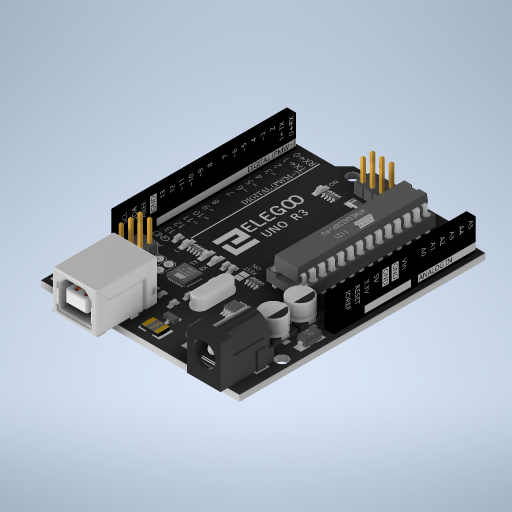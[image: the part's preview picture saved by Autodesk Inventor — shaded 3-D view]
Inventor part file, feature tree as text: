
AUTODESK INVENTOR PART (.ipt)
format: ipt  version: 2024 (Build 280153000, 153)  size: 18,753,536 bytes
history: native  units: in
note: dims shown in document units (in); Inventor stores cm internally (conversion verified against a paired STEP export)
features: other x713, projected_geometry x17, sketch x1
ambient origin geometry x8: Origin, YZ Plane, XZ Plane, XY Plane, X Axis, Y Axis, Z Axis, Center Point
bodies: Solid1 (feature_tree), Solid2 (feature_tree), Solid3 (feature_tree), Solid4 (feature_tree), Solid5 (feature_tree), Solid6 (feature_tree), Solid7 (feature_tree), Solid8 (feature_tree), Solid9 (feature_tree), Solid10 (feature_tree), Solid11 (feature_tree), Solid12 (feature_tree), Solid13 (feature_tree), Solid14 (feature_tree), Solid15 (feature_tree), Solid16 (feature_tree), Solid17 (feature_tree), Solid18 (feature_tree), Solid19 (feature_tree), Solid20 (feature_tree), Solid21 (feature_tree), Solid22 (feature_tree), Solid23 (feature_tree), Solid24 (feature_tree), Solid25 (feature_tree), Solid26 (feature_tree), Solid27 (feature_tree), Solid28 (feature_tree), Solid29 (feature_tree), Solid30 (feature_tree), Solid31 (feature_tree), Solid32 (feature_tree), Solid33 (feature_tree), Solid34 (feature_tree), Solid35 (feature_tree), Solid36 (feature_tree), Solid37 (feature_tree), Solid38 (feature_tree), Solid39 (feature_tree), Solid40 (feature_tree), Solid41 (feature_tree), Solid42 (feature_tree), Solid43 (feature_tree), Solid44 (feature_tree), Solid45 (feature_tree), Solid46 (feature_tree), Solid47 (feature_tree), Solid48 (feature_tree), Solid49 (feature_tree), Solid50 (feature_tree), Solid51 (feature_tree), Solid52 (feature_tree), Solid53 (feature_tree), Solid54 (feature_tree), Solid55 (feature_tree), Solid56 (feature_tree), Solid57 (feature_tree), Solid58 (feature_tree), Solid59 (feature_tree), Solid60 (feature_tree), Solid61 (feature_tree), Solid62 (feature_tree), Solid63 (feature_tree), Solid64 (feature_tree), Solid65 (feature_tree), Solid66 (feature_tree), Solid67 (feature_tree), Solid68 (feature_tree), Solid69 (feature_tree), Solid70 (feature_tree), Solid71 (feature_tree), Solid72 (feature_tree), Solid73 (feature_tree), Solid74 (feature_tree), Solid75 (feature_tree), Solid76 (feature_tree), Solid77 (feature_tree), Solid78 (feature_tree), Solid79 (feature_tree), Solid80 (feature_tree), Solid81 (feature_tree), Solid82 (feature_tree), Solid83 (feature_tree), Solid84 (feature_tree), Solid85 (feature_tree), Solid86 (feature_tree), Solid87 (feature_tree), Solid88 (feature_tree), Solid89 (feature_tree), Solid90 (feature_tree), Solid91 (feature_tree), Solid92 (feature_tree), Solid93 (feature_tree), Solid94 (feature_tree), Solid95 (feature_tree), Solid96 (feature_tree), Solid97 (feature_tree), Solid98 (feature_tree), Solid99 (feature_tree), Solid100 (feature_tree), Solid101 (feature_tree), Solid102 (feature_tree), Solid103 (feature_tree), Solid104 (feature_tree), Solid105 (feature_tree), Solid106 (feature_tree), Solid107 (feature_tree), Solid108 (feature_tree), Solid109 (feature_tree), Solid110 (feature_tree), Solid111 (feature_tree), Solid112 (feature_tree), Solid113 (feature_tree), Solid114 (feature_tree), Solid115 (feature_tree), Solid116 (feature_tree), Solid117 (feature_tree), Solid118 (feature_tree), Solid119 (feature_tree), Solid120 (feature_tree), Solid121 (feature_tree), Solid122 (feature_tree), Solid123 (feature_tree), Solid124 (feature_tree), Solid125 (feature_tree), Solid126 (feature_tree), Solid127 (feature_tree), Solid128 (feature_tree), Solid129 (feature_tree), Solid130 (feature_tree), Solid131 (feature_tree), Solid132 (feature_tree), Solid133 (feature_tree), Solid134 (feature_tree), Solid135 (feature_tree), Solid136 (feature_tree), Solid137 (feature_tree), Solid138 (feature_tree), Solid139 (feature_tree), Solid140 (feature_tree), Solid141 (feature_tree), Solid142 (feature_tree), Solid143 (feature_tree), Solid144 (feature_tree), Solid145 (feature_tree), Solid146 (feature_tree), Solid147 (feature_tree), Solid148 (feature_tree), Solid149 (feature_tree), Solid150 (feature_tree), Solid151 (feature_tree), Solid152 (feature_tree), Solid153 (feature_tree), Solid154 (feature_tree), Solid155 (feature_tree), Solid156 (feature_tree), Solid157 (feature_tree), Solid158 (feature_tree), Solid159 (feature_tree), Solid160 (feature_tree), Solid161 (feature_tree), Solid162 (feature_tree), Solid163 (feature_tree), Solid164 (feature_tree), Solid165 (feature_tree), Solid166 (feature_tree), Solid167 (feature_tree), Solid168 (feature_tree), Solid169 (feature_tree), Solid170 (feature_tree), Solid171 (feature_tree), Solid172 (feature_tree), Solid173 (feature_tree), Solid174 (feature_tree), Solid175 (feature_tree), Solid176 (feature_tree), Solid177 (feature_tree), Solid178 (feature_tree), Solid179 (feature_tree), Solid180 (feature_tree), Solid181 (feature_tree), Solid182 (feature_tree), Solid183 (feature_tree), Solid184 (feature_tree), Solid185 (feature_tree), Solid186 (feature_tree), Solid187 (feature_tree), Solid188 (feature_tree), Solid189 (feature_tree), Solid190 (feature_tree), Solid191 (feature_tree), Solid192 (feature_tree), Solid193 (feature_tree), Solid194 (feature_tree), Solid195 (feature_tree), Solid196 (feature_tree), Solid197 (feature_tree), Solid198 (feature_tree), Solid199 (feature_tree), Solid200 (feature_tree), Solid201 (feature_tree), Solid202 (feature_tree), Solid203 (feature_tree), Solid204 (feature_tree), Solid205 (feature_tree), Solid206 (feature_tree), Solid207 (feature_tree), Solid208 (feature_tree), Solid209 (feature_tree), Solid210 (feature_tree), Solid211 (feature_tree), Solid212 (feature_tree), Solid213 (feature_tree), Solid214 (feature_tree), Solid215 (feature_tree), Solid216 (feature_tree), Solid217 (feature_tree), Solid218 (feature_tree), Solid219 (feature_tree), Solid220 (feature_tree), Solid221 (feature_tree), Solid222 (feature_tree), Solid223 (feature_tree), Solid224 (feature_tree), Solid225 (feature_tree), Solid226 (feature_tree), Solid227 (feature_tree), Solid228 (feature_tree), Solid229 (feature_tree), Solid230 (feature_tree), Solid231 (feature_tree), Solid232 (feature_tree), Solid233 (feature_tree), Solid234 (feature_tree), Solid235 (feature_tree), Solid236 (feature_tree), Solid237 (feature_tree), Solid238 (feature_tree), Solid239 (feature_tree), Solid240 (feature_tree), Solid241 (feature_tree), Solid242 (feature_tree), Solid243 (feature_tree), Solid244 (feature_tree), Solid245 (feature_tree), Solid246 (feature_tree), Solid247 (feature_tree), Solid248 (feature_tree), Solid249 (feature_tree), Solid250 (feature_tree), Solid251 (feature_tree), Solid252 (feature_tree), Solid253 (feature_tree), Solid254 (feature_tree), Solid255 (feature_tree), Solid256 (feature_tree), Solid257 (feature_tree), Solid258 (feature_tree), Solid259 (feature_tree), Solid260 (feature_tree), Solid261 (feature_tree), Solid262 (feature_tree), Solid263 (feature_tree), Solid264 (feature_tree), Solid265 (feature_tree), Solid266 (feature_tree), Solid267 (feature_tree), Solid268 (feature_tree), Solid269 (feature_tree), Solid270 (feature_tree), Solid271 (feature_tree), Solid272 (feature_tree), Solid273 (feature_tree), Solid274 (feature_tree), Solid275 (feature_tree), Solid276 (feature_tree), Solid277 (feature_tree), Solid278 (feature_tree), Solid279 (feature_tree), Solid280 (feature_tree), Solid281 (feature_tree), Solid282 (feature_tree), Solid283 (feature_tree), Solid284 (feature_tree), Solid285 (feature_tree), Solid286 (feature_tree), Solid287 (feature_tree), Solid288 (feature_tree), Solid289 (feature_tree), Solid290 (feature_tree), Solid291 (feature_tree), Solid292 (feature_tree), Solid293 (feature_tree), Solid294 (feature_tree), Solid295 (feature_tree), Solid296 (feature_tree), Solid297 (feature_tree), Solid298 (feature_tree), Solid299 (feature_tree), Solid300 (feature_tree), Solid301 (feature_tree), Solid302 (feature_tree), Solid303 (feature_tree), Solid304 (feature_tree), Solid305 (feature_tree), Solid306 (feature_tree), Solid307 (feature_tree), Solid308 (feature_tree), Solid309 (feature_tree), Solid310 (feature_tree), Solid311 (feature_tree), Solid312 (feature_tree), Solid313 (feature_tree), Solid314 (feature_tree), Solid315 (feature_tree), Solid316 (feature_tree), Solid317 (feature_tree), Solid318 (feature_tree), Solid319 (feature_tree), Solid320 (feature_tree), Solid321 (feature_tree), Solid322 (feature_tree), Solid323 (feature_tree), Solid324 (feature_tree), Solid325 (feature_tree), Solid326 (feature_tree), Solid327 (feature_tree), Solid328 (feature_tree), Solid329 (feature_tree), Solid330 (feature_tree), Solid331 (feature_tree), Solid332 (feature_tree), Solid333 (feature_tree), Solid334 (feature_tree), Solid335 (feature_tree), Solid336 (feature_tree), Solid337 (feature_tree), Solid338 (feature_tree), Solid339 (feature_tree), Solid340 (feature_tree), Solid341 (feature_tree), Solid342 (feature_tree), Solid343 (feature_tree), Solid344 (feature_tree), Solid345 (feature_tree), Solid346 (feature_tree), Solid347 (feature_tree), Solid348 (feature_tree), Solid349 (feature_tree), Solid350 (feature_tree), Solid351 (feature_tree), Solid352 (feature_tree), Solid353 (feature_tree), Solid354 (feature_tree), Solid355 (feature_tree), Solid356 (feature_tree), Solid357 (feature_tree), Solid358 (feature_tree), Solid359 (feature_tree), Solid360 (feature_tree), Solid361 (feature_tree), Solid362 (feature_tree), Solid363 (feature_tree), Solid364 (feature_tree), Solid365 (feature_tree), Solid366 (feature_tree), Solid367 (feature_tree), Solid368 (feature_tree), Solid369 (feature_tree), Solid370 (feature_tree), Solid371 (feature_tree), Solid372 (feature_tree), Solid373 (feature_tree), Solid374 (feature_tree), Solid375 (feature_tree), Solid376 (feature_tree), Solid377 (feature_tree), Solid378 (feature_tree), Solid379 (feature_tree), Solid380 (feature_tree), Solid381 (feature_tree), Solid382 (feature_tree), Solid383 (feature_tree), Solid384 (feature_tree), Solid385 (feature_tree), Solid386 (feature_tree), Solid387 (feature_tree), Solid388 (feature_tree), Solid389 (feature_tree), Solid390 (feature_tree), Solid391 (feature_tree), Solid392 (feature_tree), Solid393 (feature_tree), Solid394 (feature_tree), Solid395 (feature_tree), Solid396 (feature_tree), Solid397 (feature_tree), Solid398 (feature_tree), Solid399 (feature_tree), Solid400 (feature_tree), Solid401 (feature_tree), Solid402 (feature_tree), Solid403 (feature_tree), Solid404 (feature_tree), Solid405 (feature_tree), Solid406 (feature_tree), Solid407 (feature_tree), Solid408 (feature_tree), Solid409 (feature_tree), Solid410 (feature_tree), Solid411 (feature_tree), Solid412 (feature_tree), Solid413 (feature_tree), Solid414 (feature_tree), Solid415 (feature_tree), Solid416 (feature_tree), Solid417 (feature_tree), Solid418 (feature_tree), Solid419 (feature_tree), Solid420 (feature_tree), Solid421 (feature_tree), Solid422 (feature_tree), Solid423 (feature_tree), Solid424 (feature_tree), Solid425 (feature_tree), Solid426 (feature_tree), Solid427 (feature_tree), Solid428 (feature_tree), Solid429 (feature_tree), Solid430 (feature_tree), Solid431 (feature_tree), Solid432 (feature_tree), Solid433 (feature_tree), Solid434 (feature_tree), Solid435 (feature_tree), Solid436 (feature_tree), Solid437 (feature_tree), Solid438 (feature_tree), Solid439 (feature_tree), Solid440 (feature_tree), Solid441 (feature_tree), Solid442 (feature_tree), Solid443 (feature_tree), Solid444 (feature_tree), Solid445 (feature_tree), Solid446 (feature_tree), Solid447 (feature_tree), Solid448 (feature_tree), Solid449 (feature_tree), Solid450 (feature_tree), Solid451 (feature_tree), Solid452 (feature_tree), Solid453 (feature_tree), Solid454 (feature_tree), Solid455 (feature_tree), Solid456 (feature_tree), Solid457 (feature_tree), Solid458 (feature_tree), Solid459 (feature_tree), Solid460 (feature_tree), Solid461 (feature_tree), Solid462 (feature_tree), Solid463 (feature_tree), Solid464 (feature_tree), Solid465 (feature_tree), Solid466 (feature_tree), Solid467 (feature_tree), Solid468 (feature_tree), Solid469 (feature_tree), Solid470 (feature_tree), Solid471 (feature_tree), Solid472 (feature_tree), Solid473 (feature_tree), Solid474 (feature_tree), Solid475 (feature_tree), Solid476 (feature_tree), Solid477 (feature_tree), Solid478 (feature_tree), Solid479 (feature_tree), Solid480 (feature_tree), Solid481 (feature_tree), Solid482 (feature_tree), Solid483 (feature_tree), Solid484 (feature_tree), Solid485 (feature_tree), Solid486 (feature_tree), Solid487 (feature_tree), Solid488 (feature_tree), Solid489 (feature_tree), Solid490 (feature_tree), Solid491 (feature_tree), Solid492 (feature_tree), Solid493 (feature_tree), Solid494 (feature_tree), Solid495 (feature_tree), Solid496 (feature_tree), Solid497 (feature_tree), Solid498 (feature_tree), Solid499 (feature_tree), Solid500 (feature_tree), Solid501 (feature_tree), Solid502 (feature_tree), Solid503 (feature_tree), Solid504 (feature_tree), Solid505 (feature_tree), Solid506 (feature_tree), Solid507 (feature_tree), Solid508 (feature_tree), Solid509 (feature_tree), Solid510 (feature_tree), Solid511 (feature_tree), Solid512 (feature_tree), Solid513 (feature_tree), Solid514 (feature_tree), Solid515 (feature_tree), Solid516 (feature_tree), Solid517 (feature_tree), Solid518 (feature_tree), Solid519 (feature_tree), Solid520 (feature_tree), Solid521 (feature_tree), Solid522 (feature_tree), Solid523 (feature_tree), Solid524 (feature_tree), Solid525 (feature_tree), Solid526 (feature_tree), Solid527 (feature_tree), Solid528 (feature_tree), Solid529 (feature_tree), Solid530 (feature_tree), Solid531 (feature_tree), Solid532 (feature_tree), Solid533 (feature_tree), Solid534 (feature_tree), Solid535 (feature_tree), Solid536 (feature_tree), Solid537 (feature_tree), Solid538 (feature_tree), Solid539 (feature_tree), Solid540 (feature_tree), Solid541 (feature_tree), Solid542 (feature_tree), Solid543 (feature_tree), Solid544 (feature_tree), Solid545 (feature_tree), Solid546 (feature_tree), Solid547 (feature_tree), Solid548 (feature_tree), Solid549 (feature_tree), Solid550 (feature_tree), Solid551 (feature_tree), Solid552 (feature_tree), Solid553 (feature_tree), Solid554 (feature_tree), Solid555 (feature_tree), Solid556 (feature_tree), Solid557 (feature_tree), Solid558 (feature_tree), Solid559 (feature_tree), Solid560 (feature_tree), Solid561 (feature_tree), Solid562 (feature_tree), Solid563 (feature_tree), Solid564 (feature_tree), Solid565 (feature_tree), Solid566 (feature_tree), Solid567 (feature_tree), Solid568 (feature_tree), Solid569 (feature_tree), Solid570 (feature_tree), Solid571 (feature_tree), Solid572 (feature_tree), Solid573 (feature_tree), Solid574 (feature_tree), Solid575 (feature_tree), Solid576 (feature_tree), Solid577 (feature_tree), Solid578 (feature_tree), Solid579 (feature_tree), Solid580 (feature_tree), Solid581 (feature_tree), Solid582 (feature_tree), Solid583 (feature_tree), Solid584 (feature_tree), Solid585 (feature_tree), Solid586 (feature_tree), Solid587 (feature_tree), Solid588 (feature_tree), Solid589 (feature_tree), Solid590 (feature_tree), Solid591 (feature_tree), Solid592 (feature_tree), Solid593 (feature_tree), Solid594 (feature_tree), Solid595 (feature_tree), Solid596 (feature_tree), Solid597 (feature_tree), Solid598 (feature_tree), Solid599 (feature_tree), Solid600 (feature_tree), Solid601 (feature_tree), Solid602 (feature_tree), Solid603 (feature_tree), Solid604 (feature_tree), Solid605 (feature_tree), Solid606 (feature_tree), Solid607 (feature_tree), Solid608 (feature_tree), Solid609 (feature_tree), Solid610 (feature_tree), Solid611 (feature_tree), Solid612 (feature_tree), Solid613 (feature_tree), Solid614 (feature_tree), Solid615 (feature_tree), Solid616 (feature_tree), Solid617 (feature_tree), Solid618 (feature_tree), Solid619 (feature_tree), Solid620 (feature_tree), Solid621 (feature_tree), Solid622 (feature_tree), Solid623 (feature_tree), Solid624 (feature_tree), Solid625 (feature_tree), Solid626 (feature_tree), Solid627 (feature_tree), Solid628 (feature_tree), Solid629 (feature_tree), Solid630 (feature_tree), Solid631 (feature_tree), Solid632 (feature_tree), Solid633 (feature_tree), Solid634 (feature_tree), Solid635 (feature_tree), Solid636 (feature_tree), Solid637 (feature_tree), Solid638 (feature_tree), Solid639 (feature_tree), Solid640 (feature_tree), Solid641 (feature_tree), Solid642 (feature_tree), Solid643 (feature_tree), Solid644 (feature_tree), Solid645 (feature_tree), Solid646 (feature_tree), Solid647 (feature_tree), Solid648 (feature_tree), Solid649 (feature_tree), Solid650 (feature_tree), Solid651 (feature_tree), Solid652 (feature_tree), Solid653 (feature_tree), Solid654 (feature_tree), Solid655 (feature_tree), Solid656 (feature_tree), Solid657 (feature_tree), Solid658 (feature_tree), Solid659 (feature_tree), Solid660 (feature_tree), Solid661 (feature_tree), Solid662 (feature_tree), Solid663 (feature_tree), Solid664 (feature_tree), Solid665 (feature_tree), Solid666 (feature_tree), Solid667 (feature_tree), Solid668 (feature_tree), Solid669 (feature_tree), Solid670 (feature_tree), Solid671 (feature_tree), Solid672 (feature_tree), Solid673 (feature_tree), Solid674 (feature_tree), Solid675 (feature_tree), Solid676 (feature_tree), Solid677 (feature_tree), Solid678 (feature_tree), Solid679 (feature_tree), Solid680 (feature_tree), Solid681 (feature_tree), Solid682 (feature_tree), Solid683 (feature_tree), Solid684 (feature_tree), Solid685 (feature_tree), Solid686 (feature_tree), Solid687 (feature_tree), Solid688 (feature_tree), Solid689 (feature_tree), Solid690 (feature_tree), Solid691 (feature_tree), Solid692 (feature_tree), Solid693 (feature_tree), Solid694 (feature_tree), Solid695 (feature_tree), Solid696 (feature_tree), Solid697 (feature_tree), Solid698 (feature_tree), Solid699 (feature_tree), Solid700 (feature_tree), Solid701 (feature_tree), Solid702 (feature_tree), Solid703 (feature_tree), Solid704 (feature_tree), Solid705 (feature_tree), Solid706 (feature_tree), Solid707 (feature_tree), Solid708 (feature_tree), Solid709 (feature_tree), Solid710 (feature_tree), Solid711 (feature_tree), Solid712 (feature_tree), Solid713 (feature_tree)
feature tree (731):
  sketch  "Sketch1"
  projected_geometry  "Projected Loop1"
  projected_geometry  "Projected Loop2"
  projected_geometry  "Projected Loop3"
  projected_geometry  "Projected Loop4"
  projected_geometry  "Projected Loop5"
  projected_geometry  "Projected Loop6"
  projected_geometry  "Projected Loop7"
  projected_geometry  "Projected Loop8"
  projected_geometry  "Projected Loop9"
  projected_geometry  "Projected Loop10"
  projected_geometry  "Projected Loop11"
  projected_geometry  "Projected Loop12"
  projected_geometry  "Projected Loop13"
  projected_geometry  "Projected Loop14"
  projected_geometry  "Projected Loop15"
  projected_geometry  "Projected Loop16"
  projected_geometry  "Projected Loop17"
  other  "I_O Headers"
  other  "I_O Headers:1"
  other  "I_O Headers:2"
  other  "I_O Headers:3"
  other  "I_O Headers:4"
  other  "I_O Headers:5"
  other  "I_O Headers:6"
  other  "I_O Headers:7"
  other  "I_O Headers:8"
  other  "I_O Headers:9"
  other  "I_O Headers:10"
  other  "I_O Headers:11"
  other  "I_O Headers:12"
  other  "I_O Headers:13"
  other  "I_O Headers:14"
  other  "I_O Headers:15"
  other  "I_O Headers:16"
  other  "I_O Headers:17"
  other  "I_O Headers:18"
  other  "I_O Headers:19"
  other  "I_O Headers:20"
  other  "I_O Headers:21"
  other  "I_O Headers:22"
  other  "I_O Headers:23"
  other  "I_O Headers:24"
  other  "I_O Headers:25"
  other  "I_O Headers:26"
  other  "I_O Headers:27"
  other  "I_O Headers:28"
  other  "I_O Headers:29"
  other  "I_O Headers:30"
  other  "I_O Headers:31"
  other  "I_O Headers:32"
  other  "I_O Headers:33"
  other  "I_O Headers:34"
  other  "I_O Headers:35"
  other  "I_O Headers:36"
  other  "I_O Headers:37"
  other  "I_O Headers:38"
  other  "I_O Headers:39"
  other  "I_O Headers:40"
  other  "I_O Headers:41"
  other  "I_O Headers:42"
  other  "I_O Headers:43"
  other  "I_O Headers:44"
  other  "I_O Headers:45"
  other  "I_O Headers:46"
  other  "I_O Headers:47"
  other  "I_O Headers:48"
  other  "I_O Headers:49"
  other  "I_O Headers:50"
  other  "I_O Headers:51"
  other  "I_O Headers:52"
  other  "I_O Headers:53"
  other  "I_O Headers:54"
  other  "I_O Headers:55"
  other  "I_O Headers:56"
  other  "I_O Headers:57"
  other  "I_O Headers:58"
  other  "I_O Headers:59"
  other  "I_O Headers:60"
  other  "I_O Headers:61"
  other  "I_O Headers:62"
  other  "I_O Headers:63"
  other  "I_O Headers:64"
  other  "I_O Headers:65"
  other  "I_O Headers:66"
  other  "I_O Headers:67"
  other  "I_O Headers:68"
  other  "I_O Headers:69"
  other  "I_O Headers:70"
  other  "I_O Headers:71"
  other  "I_O Headers:72"
  other  "I_O Headers:73"
  other  "I_O Headers:74"
  other  "I_O Headers:75"
  other  "I_O Headers:76"
  other  "I_O Headers:77"
  other  "I_O Headers:78"
  other  "I_O Headers:79"
  other  "I_O Headers:80"
  other  "I_O Headers:81"
  other  "I_O Headers:82"
  other  "I_O Headers:83"
  other  "I_O Headers:84"
  other  "I_O Headers:85"
  other  "I_O Headers:86"
  other  "I_O Headers:87"
  other  "I_O Headers:88"
  other  "I_O Headers:89"
  other  "I_O Headers:90"
  other  "I_O Headers:91"
  other  "I_O Headers:92"
  other  "I_O Headers:93"
  other  "I_O Headers:94"
  other  "I_O Headers:95"
  other  "I_O Headers:96"
  other  "I_O Headers:97"
  other  "I_O Headers:98"
  other  "I_O Headers:99"
  other  "I_O Headers:100"
  other  "I_O Headers:101"
  other  "I_O Headers:102"
  other  "I_O Headers:103"
  other  "I_O Headers:104"
  other  "I_O Headers:105"
  other  "I_O Headers:106"
  other  "I_O Headers:107"
  other  "I_O Headers:108"
  other  "I_O Headers:109"
  other  "I_O Headers:110"
  other  "I_O Headers:111"
  other  "I_O Headers:112"
  other  "I_O Headers:113"
  other  "I_O Headers:114"
  other  "I_O Headers:115"
  other  "I_O Headers:116"
  other  "I_O Headers:117"
  other  "I_O Headers:118"
  other  "I_O Headers:119"
  other  "I_O Headers:120"
  other  "I_O Headers:121"
  other  "I_O Headers:122"
  other  "I_O Headers:123"
  other  "I_O Headers:124"
  other  "I_O Headers:125"
  other  "I_O Headers:126"
  other  "I_O Headers:127"
  other  "I_O Headers:128"
  other  "I_O Headers:129"
  other  "I_O Headers:130"
  other  "I_O Headers:131"
  other  "I_O Headers:132"
  other  "I_O Headers:133"
  other  "I_O Headers:134"
  other  "I_O Headers:135"
  other  "I_O Headers:136"
  other  "I_O Headers:137"
  other  "I_O Headers:138"
  other  "I_O Headers:139"
  other  "I_O Headers:140"
  other  "I_O Headers:141"
  other  "I_O Headers:142"
  other  "I_O Headers:143"
  other  "I_O Headers:144"
  other  "I_O Headers:145"
  other  "I_O Headers:146"
  other  "I_O Headers:147"
  other  "I_O Headers:148"
  other  "I_O Headers:149"
  other  "I_O Headers:150"
  other  "I_O Headers:151"
  other  "I_O Headers:152"
  other  "I_O Headers:153"
  other  "I_O Headers:154"
  other  "I_O Headers:155"
  other  "I_O Headers:156"
  other  "I_O Headers:157"
  other  "I_O Headers:158"
  other  "I_O Headers:159"
  other  "I_O Headers:160"
  other  "I_O Headers:161"
  other  "I_O Headers:162"
  other  "I_O Headers:163"
  other  "I_O Headers:164"
  other  "I_O Headers:165"
  other  "I_O Headers:166"
  other  "I_O Headers:167"
  other  "I_O Headers:168"
  other  "I_O Headers:169"
  other  "I_O Headers:170"
  other  "I_O Headers:171"
  other  "I_O Headers:172"
  other  "I_O Headers:173"
  other  "I_O Headers:174"
  other  "I_O Headers:175"
  other  "I_O Headers:176"
  other  "I_O Headers:177"
  other  "I_O Headers:178"
  other  "I_O Headers:179"
  other  "I_O Headers:180"
  other  "I_O Headers:181"
  other  "I_O Headers:182"
  other  "I_O Headers:183"
  other  "I_O Headers:184"
  other  "I_O Headers:185"
  other  "I_O Headers:186"
  other  "I_O Headers:187"
  other  "I_O Headers:188"
  other  "I_O Headers:189"
  other  "I_O Headers:190"
  other  "I_O Headers:191"
  other  "I_O Headers:192"
  other  "I_O Headers:193"
  other  "I_O Headers:194"
  other  "I_O Headers:195"
  other  "I_O Headers:196"
  other  "I_O Headers:197"
  other  "I_O Headers:198"
  other  "I_O Headers:199"
  other  "I_O Headers:200"
  other  "I_O Headers:201"
  other  "I_O Headers:202"
  other  "I_O Headers:203"
  other  "I_O Headers:204"
  other  "I_O Headers:205"
  other  "I_O Headers:206"
  other  "I_O Headers:207"
  other  "I_O Headers:208"
  other  "I_O Headers:209"
  other  "brep_211"
  other  "brep_212"
  other  "brep_213"
  other  "brep_214"
  other  "brep_215"
  other  "brep_216"
  other  "brep_217"
  other  "brep_218"
  other  "brep_219"
  other  "brep_220"
  other  "brep_221"
  other  "brep_222"
  other  "brep_223"
  other  "brep_224"
  other  "brep_225"
  other  "brep_226"
  other  "brep_227"
  other  "brep_228"
  other  "brep_229"
  other  "brep_230"
  other  "brep_231"
  other  "brep_232"
  other  "brep_233"
  other  "brep_234"
  other  "brep_235"
  other  "brep_236"
  other  "brep_237"
  other  "brep_238"
  other  "brep_239"
  other  "brep_240"
  other  "brep_241"
  other  "brep_242"
  other  "brep_243"
  other  "brep_244"
  other  "brep_245"
  other  "brep_246"
  other  "brep_247"
  other  "brep_248"
  other  "brep_249"
  other  "brep_250"
  other  "brep_251"
  other  "brep_252"
  other  "brep_253"
  other  "brep_254"
  other  "brep_255"
  other  "brep_256"
  other  "brep_257"
  other  "brep_258"
  other  "brep_259"
  other  "brep_260"
  other  "brep_261"
  other  "brep_262"
  other  "brep_263"
  other  "brep_264"
  other  "brep_265"
  other  "brep_266"
  other  "brep_267"
  other  "brep_268"
  other  "brep_269"
  other  "brep_270"
  other  "brep_271"
  other  "brep_272"
  other  "brep_273"
  other  "brep_274"
  other  "brep_275"
  other  "brep_276"
  other  "brep_277"
  other  "brep_278"
  other  "brep_279"
  other  "brep_280"
  other  "brep_281"
  other  "brep_282"
  other  "brep_283"
  other  "brep_284"
  other  "brep_285"
  other  "brep_286"
  other  "brep_287"
  other  "brep_288"
  other  "brep_289"
  other  "brep_290"
  other  "brep_291"
  other  "brep_292"
  other  "brep_293"
  other  "brep_294"
  other  "brep_295"
  other  "brep_296"
  other  "brep_297"
  other  "brep_298"
  other  "brep_299"
  other  "brep_300"
  other  "brep_301"
  other  "brep_302"
  other  "brep_303"
  other  "brep_304"
  other  "brep_305"
  other  "brep_306"
  other  "brep_307"
  other  "brep_308"
  other  "brep_309"
  other  "brep_310"
  other  "brep_311"
  other  "brep_312"
  other  "brep_313"
  other  "brep_314"
  other  "brep_315"
  other  "brep_316"
  other  "brep_317"
  other  "brep_318"
  other  "brep_319"
  other  "brep_320"
  other  "brep_321"
  other  "brep_322"
  other  "brep_323"
  other  "brep_324"
  other  "brep_325"
  other  "brep_326"
  other  "brep_327"
  other  "brep_328"
  other  "brep_329"
  other  "brep_330"
  other  "brep_331"
  other  "brep_332"
  other  "brep_333"
  other  "brep_334"
  other  "brep_335"
  other  "brep_336"
  other  "brep_337"
  other  "brep_338"
  other  "brep_339"
  other  "brep_340"
  other  "brep_341"
  other  "brep_342"
  other  "brep_343"
  other  "brep_344"
  other  "brep_345"
  other  "brep_346"
  other  "brep_347"
  other  "brep_348"
  other  "brep_349"
  other  "brep_350"
  other  "brep_351"
  other  "brep_352"
  other  "brep_353"
  other  "brep_354"
  other  "brep_355"
  other  "brep_356"
  other  "brep_357"
  other  "brep_358"
  other  "brep_359"
  other  "brep_360"
  other  "brep_361"
  other  "brep_362"
  other  "brep_363"
  other  "brep_364"
  other  "brep_365"
  other  "brep_366"
  other  "brep_367"
  other  "brep_368"
  other  "brep_369"
  other  "brep_370"
  other  "brep_371"
  other  "brep_372"
  other  "brep_373"
  other  "brep_374"
  other  "brep_375"
  other  "brep_376"
  other  "brep_377"
  other  "brep_378"
  other  "brep_379"
  other  "brep_380"
  other  "brep_381"
  other  "brep_382"
  other  "brep_383"
  other  "brep_384"
  other  "brep_385"
  other  "brep_386"
  other  "brep_387"
  other  "brep_388"
  other  "brep_389"
  other  "USB Interface Chip"
  other  "USB Interface Chip:1"
  other  "USB Interface Chip:2"
  other  "USB Interface Chip:3"
  other  "USB Interface Chip:4"
  other  "USB Interface Chip:5"
  other  "USB Interface Chip:6"
  other  "USB Interface Chip:7"
  other  "USB Interface Chip:8"
  other  "USB Interface Chip:9"
  other  "USB Interface Chip:10"
  other  "USB Interface Chip:11"
  other  "USB Interface Chip:12"
  other  "USB Interface Chip:13"
  other  "USB Interface Chip:14"
  other  "USB Interface Chip:15"
  other  "USB Interface Chip:16"
  other  "USB Interface Chip:17"
  other  "USB Interface Chip:18"
  other  "USB Interface Chip:19"
  other  "USB Interface Chip:20"
  other  "USB Interface Chip:21"
  other  "USB Interface Chip:22"
  other  "USB Interface Chip:23"
  other  "USB Interface Chip:24"
  other  "USB Interface Chip:25"
  other  "USB Interface Chip:26"
  other  "USB Interface Chip:27"
  other  "USB Interface Chip:28"
  other  "USB Interface Chip:29"
  other  "USB Interface Chip:30"
  other  "USB Interface Chip:31"
  other  "USB Interface Chip:32"
  other  "USB Interface Chip:33"
  other  "USB Interface Chip:34"
  other  "USB Interface Chip:35"
  other  "USB Interface Chip:36"
  other  "USB Interface Chip:37"
  other  "USB Interface Chip:38"
  other  "USB Interface Chip:39"
  other  "USB Interface Chip:40"
  other  "USB Interface Chip:41"
  other  "USB Interface Chip:42"
  other  "USB Interface Chip:43"
  other  "USB Interface Chip:44"
  other  "USB Interface Chip:45"
  other  "USB Interface Chip:46"
  other  "USB Interface Chip:47"
  other  "USB Interface Chip:48"
  other  "USB Interface Chip:49"
  other  "USB Interface Chip:50"
  other  "USB Interface Chip:51"
  other  "USB Interface Chip:52"
  other  "USB Interface Chip:53"
  other  "USB Interface Chip:54"
  other  "USB Interface Chip:55"
  other  "USB Interface Chip:56"
  other  "USB Interface Chip:57"
  other  "USB Interface Chip:58"
  other  "USB Interface Chip:59"
  other  "brep_450"
  other  "brep_451"
  other  "brep_452"
  other  "brep_453"
  other  "brep_454"
  other  "brep_455"
  other  "brep_456"
  other  "brep_457"
  other  "brep_458"
  other  "brep_459"
  other  "brep_460"
  other  "brep_461"
  other  "brep_462"
  other  "brep_463"
  other  "brep_464"
  other  "brep_465"
  other  "brep_466"
  other  "brep_467"
  other  "brep_468"
  other  "brep_469"
  other  "brep_470"
  other  "brep_471"
  other  "brep_472"
  other  "I_O Headers:210"
  other  "I_O Headers:211"
  other  "I_O Headers:212"
  other  "I_O Headers:213"
  other  "I_O Headers:214"
  other  "I_O Headers:215"
  other  "I_O Headers:216"
  other  "I_O Headers:217"
  other  "I_O Headers:218"
  other  "brep_482"
  other  "brep_483"
  other  "brep_484"
  other  "brep_485"
  other  "brep_486"
  other  "brep_487"
  other  "brep_488"
  other  "brep_489"
  other  "brep_490"
  other  "brep_491"
  other  "brep_492"
  other  "brep_493"
  other  "brep_494"
  other  "brep_495"
  other  "brep_496"
  other  "brep_497"
  other  "brep_498"
  other  "brep_499"
  other  "brep_500"
  other  "brep_501"
  other  "brep_502"
  other  "brep_503"
  other  "brep_504"
  other  "brep_505"
  other  "brep_506"
  other  "brep_507"
  other  "brep_508"
  other  "brep_509"
  other  "brep_510"
  other  "Pin 13 LED"
  other  "Pin 13 LED:1"
  other  "Pin 13 LED:2"
  other  "TX LED"
  other  "TX LED:1"
  other  "TX LED:2"
  other  "RX LED"
  other  "RX LED:1"
  other  "RX LED:2"
  other  "brep_520"
  other  "brep_521"
  other  "brep_522"
  other  "brep_523"
  other  "brep_524"
  other  "brep_525"
  other  "brep_526"
  other  "brep_527"
  other  "brep_528"
  other  "brep_529"
  other  "brep_530"
  other  "brep_531"
  other  "brep_532"
  other  "brep_533"
  other  "brep_534"
  other  "brep_535"
  other  "brep_536"
  other  "brep_537"
  other  "brep_538"
  other  "Power LED"
  other  "Power LED:1"
  other  "Power LED:2"
  other  "I_O Headers:219"
  other  "I_O Headers:220"
  other  "I_O Headers:221"
  other  "I_O Headers:222"
  other  "I_O Headers:223"
  other  "I_O Headers:224"
  other  "I_O Headers:225"
  other  "I_O Headers:226"
  other  "I_O Headers:227"
  other  "Atmega 328P Microcontroller"
  other  "Atmega 328P Microcontroller:1"
  other  "Atmega 328P Microcontroller:2"
  other  "Atmega 328P Microcontroller:3"
  other  "Atmega 328P Microcontroller:4"
  other  "Atmega 328P Microcontroller:5"
  other  "Atmega 328P Microcontroller:6"
  other  "Atmega 328P Microcontroller:7"
  other  "Atmega 328P Microcontroller:8"
  other  "Atmega 328P Microcontroller:9"
  other  "Atmega 328P Microcontroller:10"
  other  "Atmega 328P Microcontroller:11"
  other  "Atmega 328P Microcontroller:12"
  other  "Atmega 328P Microcontroller:13"
  other  "Atmega 328P Microcontroller:14"
  other  "Atmega 328P Microcontroller:15"
  other  "Atmega 328P Microcontroller:16"
  other  "Atmega 328P Microcontroller:17"
  other  "Atmega 328P Microcontroller:18"
  other  "Atmega 328P Microcontroller:19"
  other  "Atmega 328P Microcontroller:20"
  other  "Atmega 328P Microcontroller:21"
  other  "Atmega 328P Microcontroller:22"
  other  "Atmega 328P Microcontroller:23"
  other  "Atmega 328P Microcontroller:24"
  other  "Atmega 328P Microcontroller:25"
  other  "Atmega 328P Microcontroller:26"
  other  "Atmega 328P Microcontroller:27"
  other  "I_O Headers:228"
  other  "I_O Headers:229"
  other  "I_O Headers:230"
  other  "I_O Headers:231"
  other  "I_O Headers:232"
  other  "I_O Headers:233"
  other  "I_O Headers:234"
  other  "I_O Headers:235"
  other  "I_O Headers:236"
  other  "I_O Headers:237"
  other  "I_O Headers:238"
  other  "I_O Headers:239"
  other  "I_O Headers:240"
  other  "I_O Headers:241"
  other  "brep_593"
  other  "brep_594"
  other  "brep_595"
  other  "brep_596"
  other  "brep_597"
  other  "brep_598"
  other  "brep_599"
  other  "brep_600"
  other  "brep_601"
  other  "brep_602"
  other  "brep_603"
  other  "brep_604"
  other  "brep_605"
  other  "brep_606"
  other  "brep_607"
  other  "brep_608"
  other  "brep_609"
  other  "brep_610"
  other  "brep_611"
  other  "brep_612"
  other  "brep_613"
  other  "5.5mm DC Barrel Jack"
  other  "5.5mm DC Barrel Jack:1"
  other  "5.5mm DC Barrel Jack:2"
  other  "5.5mm DC Barrel Jack:3"
  other  "5.5mm DC Barrel Jack:4"
  other  "Voltage Regulator"
  other  "Voltage Regulator:1"
  other  "Voltage Regulator:2"
  other  "Voltage Regulator:3"
  other  "Voltage Regulator:4"
  other  "brep_624"
  other  "brep_625"
  other  "brep_626"
  other  "brep_627"
  other  "brep_628"
  other  "brep_629"
  other  "brep_630"
  other  "Reset Button"
  other  "Reset Button:1"
  other  "brep_633"
  other  "brep_634"
  other  "brep_635"
  other  "brep_636"
  other  "brep_637"
  other  "brep_638"
  other  "brep_639"
  other  "brep_640"
  other  "brep_641"
  other  "brep_642"
  other  "brep_643"
  other  "brep_644"
  other  "brep_645"
  other  "brep_646"
  other  "brep_647"
  other  "brep_648"
  other  "brep_649"
  other  "brep_650"
  other  "brep_651"
  other  "brep_652"
  other  "brep_653"
  other  "brep_654"
  other  "brep_655"
  other  "brep_656"
  other  "5.5mm DC Barrel Jack:5"
  other  "brep_658"
  other  "Crystal Oscillator"
  other  "Atmega 328P Microcontroller:28"
  other  "Atmega 328P Microcontroller:29"
  other  "Atmega 328P Microcontroller:30"
  other  "Atmega 328P Microcontroller:31"
  other  "Atmega 328P Microcontroller:32"
  other  "Atmega 328P Microcontroller:33"
  other  "Atmega 328P Microcontroller:34"
  other  "Atmega 328P Microcontroller:35"
  other  "Atmega 328P Microcontroller:36"
  other  "Atmega 328P Microcontroller:37"
  other  "brep_670"
  other  "brep_671"
  other  "brep_672"
  other  "brep_673"
  other  "brep_674"
  other  "brep_675"
  other  "brep_676"
  other  "brep_677"
  other  "brep_678"
  other  "USB"
  other  "USB:1"
  other  "USB:2"
  other  "USB:3"
  other  "USB:4"
  other  "USB:5"
  other  "brep_685"
  other  "brep_686"
  other  "brep_687"
  other  "brep_688"
  other  "brep_689"
  other  "brep_690"
  other  "brep_691"
  other  "brep_692"
  other  "brep_693"
  other  "brep_694"
  other  "brep_695"
  other  "brep_696"
  other  "brep_697"
  other  "brep_698"
  other  "brep_699"
  other  "brep_700"
  other  "brep_701"
  other  "brep_702"
  other  "brep_703"
  other  "brep_704"
  other  "brep_705"
  other  "brep_706"
  other  "brep_707"
  other  "brep_708"
  other  "brep_709"
  other  "brep_710"
  other  "brep_711"
  other  "brep_712"
  other  "brep_713"
